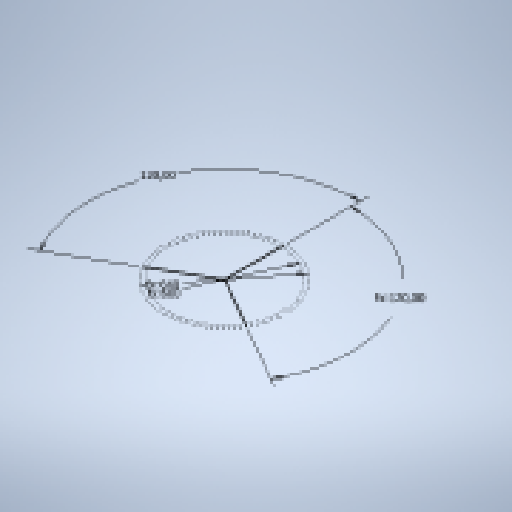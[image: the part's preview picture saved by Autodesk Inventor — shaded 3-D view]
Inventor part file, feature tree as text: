
AUTODESK INVENTOR PART (.ipt)
format: ipt  version: 2025 (Build 290162010, 162A)  size: 133,632 bytes
history: native  units: mm
features: sketch x1
ambient origin geometry x8: Origin, YZ Plane, XZ Plane, XY Plane, X Axis, Y Axis, Z Axis, Center Point
feature tree (1):
  sketch  "Sketch1"  dims[d1=600.0mm d2=120.0deg d3=120.0deg d4=640.0mm]
